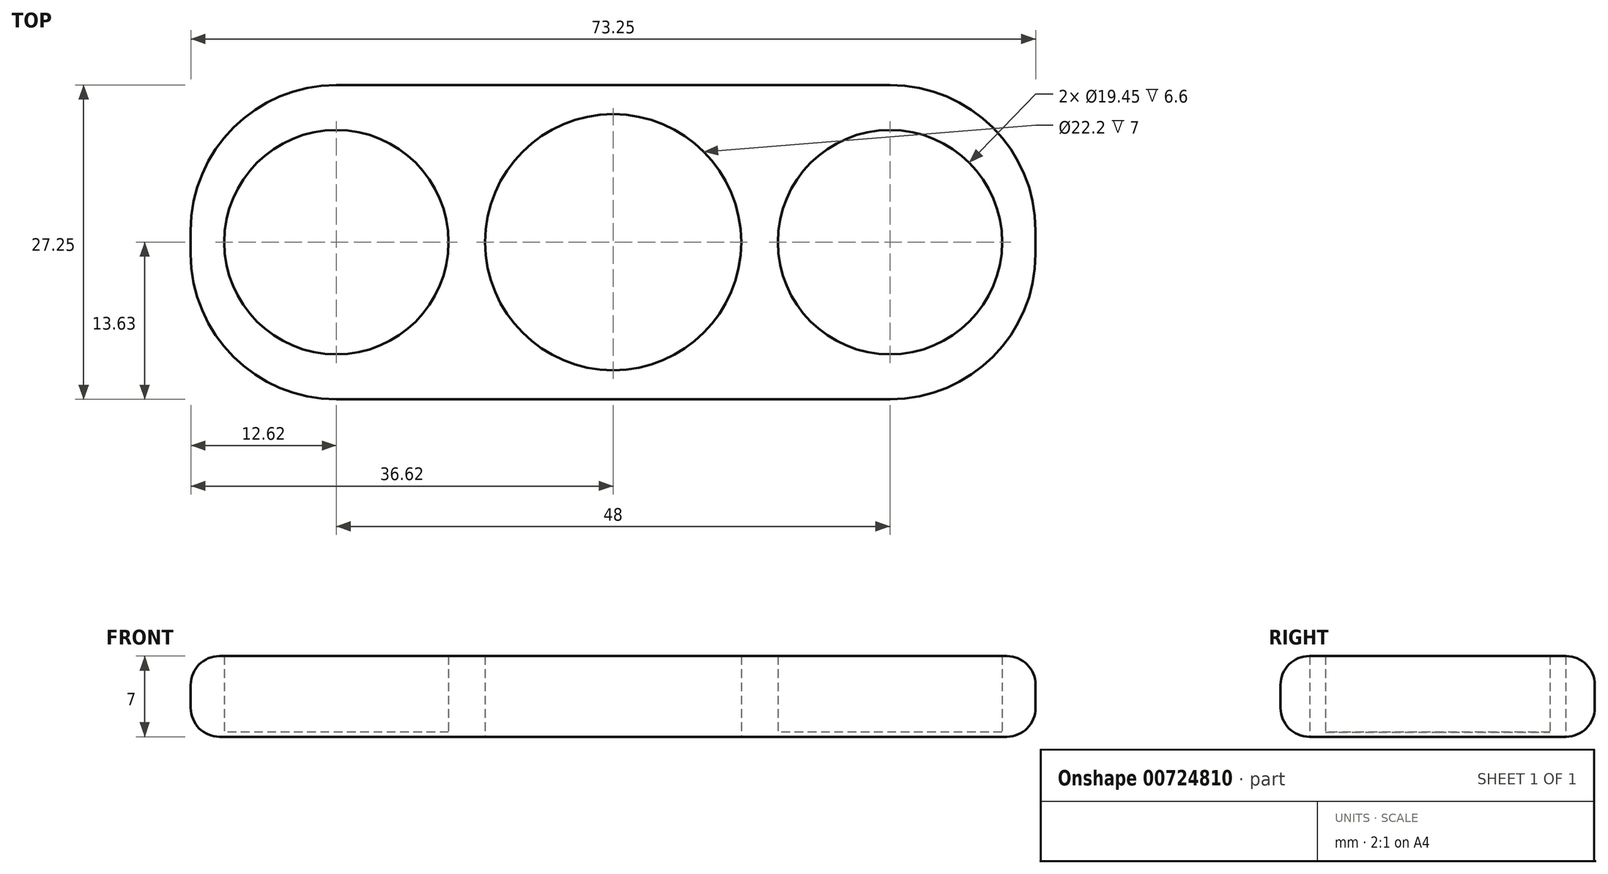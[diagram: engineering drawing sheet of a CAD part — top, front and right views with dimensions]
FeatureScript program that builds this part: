
annotation { "Feature Type Name" : "Feature", "Feature Type Description" : "" }
export const myFeature = defineFeature(function(context is Context, id is Id, definition is map)
    precondition{}
    {
        {
            var Q0;
            Q0=qCreatedBy(makeId("Top.planeOp"),FACE);
            var sketch = newSketch(context, id + "F0", { "sketchPlane" : qUnion([Q0])});
            skCircle(sketch, "E0", {"center": v(0, 0) * mm, "radius": 11.1 * mm});
            skCircle(sketch, "E1", {"center": v(-24, 0) * mm, "radius": 9.72 * mm});
            skCircle(sketch, "E2", {"center": v(24, 0) * mm, "radius": 9.72 * mm});
            skLineSegment(sketch, "E3.bottom", {"start": v(-24, 13.62) * mm, "end": v(24, 13.63) * mm});
            skLineSegment(sketch, "E3.top", {"start": v(-24, -13.63) * mm, "end": v(24, -13.62) * mm});
            skLineSegment(sketch, "E3.left", {"start": v(-36.62, 1) * mm, "end": v(-36.62, -1) * mm});
            skLineSegment(sketch, "E3.right", {"start": v(36.62, 1) * mm, "end": v(36.62, -1) * mm});
            skPoint(sketch, "E4.visualSharp", {"position": v(-36.62, 13.62) * mm});
            skArc(sketch, "E4.filletArc", {"start": v(-24, 13.62) * mm, "mid": v(-32.93, 9.93) * mm, "end": v(-36.62, 1) * mm});
            skPoint(sketch, "E5.visualSharp", {"position": v(-36.62, -13.63) * mm});
            skArc(sketch, "E5.filletArc", {"start": v(-36.62, -1) * mm, "mid": v(-32.93, -9.93) * mm, "end": v(-24, -13.63) * mm});
            skPoint(sketch, "E6.visualSharp", {"position": v(36.62, 13.63) * mm});
            skArc(sketch, "E6.filletArc", {"start": v(36.62, 1) * mm, "mid": v(32.93, 9.93) * mm, "end": v(24, 13.63) * mm});
            skPoint(sketch, "E7.visualSharp", {"position": v(36.62, -13.62) * mm});
            skArc(sketch, "E7.filletArc", {"start": v(24, -13.62) * mm, "mid": v(32.93, -9.93) * mm, "end": v(36.62, -1) * mm});
            skSolve(sketch);
        }
        {
            var Q0;
            Q0=qSketchRegion(id+"F0",true);
            extrude(context, id + "F1", {"entities" : qUnion([Q0]), "depth" : 7 * mm, "offsetDistance" : 25 * mm});
        }
        {
            var Q0;
            Q0=makeQuery(id+"F1.opExtrude","CAP_EDGE",EDGE,{"disambiguationData":[OSD([sQuery(id+"F0.wireOp",EDGE,"E3.top")])],"isStart":false});
            var Q1;
            Q1=makeQuery(id+"F1.opExtrude","CAP_EDGE",EDGE,{"disambiguationData":[OSD([sQuery(id+"F0.wireOp",EDGE,"E3.top")])],"isStart":true});
            fillet(context, id + "F2", {"entities" : qUnion([Q0, Q1]), "radius" : 2.5 * mm, "tangentPropagation" : true, "allowEdgeOverflow" : false});
        }
        {
            var Q0;
            Q0=qCreatedBy(makeId("Top.planeOp"),FACE);
            var sketch = newSketch(context, id + "F3", { "sketchPlane" : qUnion([Q0])});
            skCircle(sketch, "E8", {"center": v(-24, 0) * mm, "radius": 9.75 * mm});
            skCircle(sketch, "E9", {"center": v(24, 0) * mm, "radius": 9.75 * mm});
            skSolve(sketch);
        }
        {
            var Q0;
            Q0=qSketchRegion(id+"F3",true);
            extrude(context, id + "F4", {"entities" : qUnion([Q0]), "operationType" : NewBodyOperationType.ADD, "depth" : .4 * mm, "offsetDistance" : 25 * mm});
        }
    });
